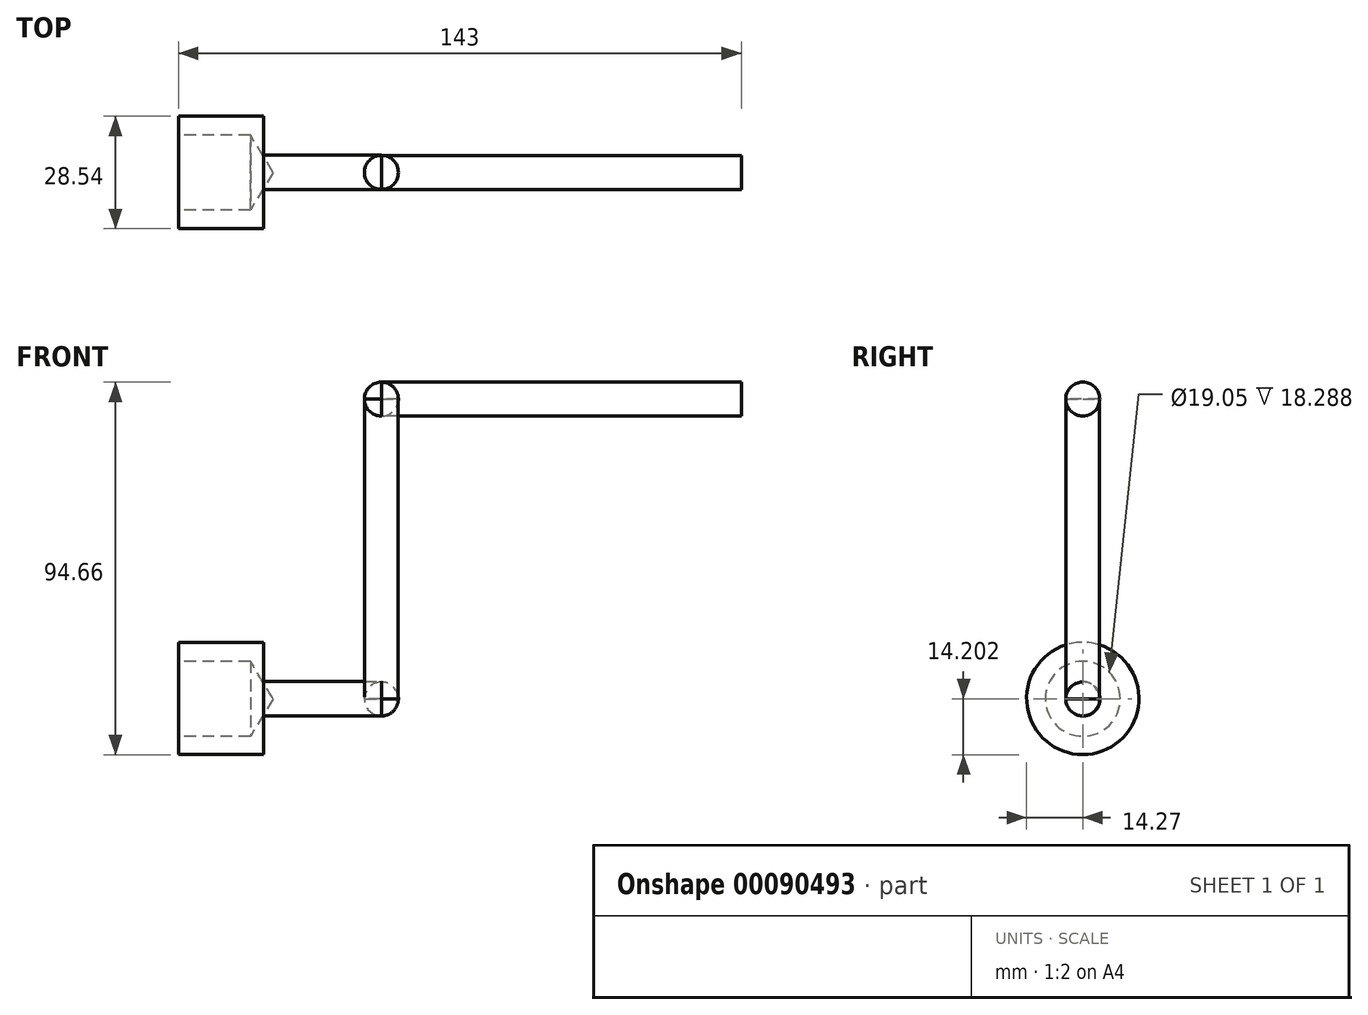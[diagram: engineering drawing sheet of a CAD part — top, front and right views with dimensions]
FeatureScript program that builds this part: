
annotation { "Feature Type Name" : "Feature", "Feature Type Description" : "" }
export const myFeature = defineFeature(function(context is Context, id is Id, definition is map)
    precondition{}
    {
        {
            var Q0;
            Q0=qCreatedBy(makeId("Right.planeOp"),FACE);
            var sketch = newSketch(context, id + "F0", { "sketchPlane" : qUnion([Q0])});
            skCircle(sketch, "E0", {"center": v(0, 45.27) * mm, "radius": 4.32 * mm});
            skLineSegment(sketch, "E1", {"start": v(0, 40.95) * mm, "end": v(0, 49.59) * mm});
            skSolve(sketch);
        }
        {
            var Q0;
            Q0=qCreatedBy(makeId("Right.planeOp"),FACE);
            cPlane(context, id + "F1", {"entities" : qUnion([Q0]), "cplaneType" : CPlaneType.OFFSET, "offset" : 91.44 * mm, "width" : 152.4 * mm, "height" : 152.4 * mm});
        }
        {
            var Q0;
            Q0=qCreatedBy(id+"F1.planeOp",FACE);
            var sketch = newSketch(context, id + "F2", { "sketchPlane" : qUnion([Q0])});
            skCircle(sketch, "E2", {"center": v(0.04, 45.27) * mm, "radius": 3.16 * mm});
            skPoint(sketch, "E2.first.point", {"position": v(0, 48.43) * mm});
            skPoint(sketch, "E2.second.point", {"position": v(0, 42.11) * mm});
            skPoint(sketch, "E2.third.point", {"position": v(3.16, 45.8) * mm});
            skSolve(sketch);
        }
        {
            var Q0;
            {var subQ0=sQuery(id+"F0.wireOp",EDGE,"E1");Q0=makeQuery(id+"F0.imprint","IMPRINT",FACE,{"disambiguationData":[TD([[makeQuery(id+"F0.imprint","IMPRINT",EDGE,{"derivedFrom":subQ0}),-1.0]])]});}
            var Q1;
            {var subQ0=sQuery(id+"F0.wireOp",EDGE,"E1");Q1=makeQuery(id+"F0.imprint","IMPRINT",FACE,{"disambiguationData":[TD([[makeQuery(id+"F0.imprint","IMPRINT",EDGE,{"derivedFrom":subQ0}),1.0]])]});}
            var Q2;
            Q2=sQuery(id+"F0.wireOp",EDGE,"E0");
            extrude(context, id + "F3", {"entities" : qUnion([Q0, Q1]), "surfaceEntities" : qUnion([Q2]), "depth" : 91.44 * mm});
        }
        {
            var Q0;
            {var subQ0=sQuery(id+"F0.wireOp",EDGE,"E1");Q0=makeQuery(id+"F0.imprint","IMPRINT",FACE,{"disambiguationData":[TD([[makeQuery(id+"F0.imprint","IMPRINT",EDGE,{"derivedFrom":subQ0}),1.0]])]});}
            var Q1;
            Q1=sQuery(id+"F0.wireOp",EDGE,"E1");
            revolve(context, id + "F4", {"entities" : qUnion([Q0]), "axis" : qUnion([Q1]), "revolveType" : RevolveType.FULL});
        }
        {
            var Q0;
            Q0=qCreatedBy(makeId("Top.planeOp"),FACE);
            cPlane(context, id + "F5", {"entities" : qUnion([Q0]), "cplaneType" : CPlaneType.OFFSET, "offset" : 45.27 * mm, "width" : 152.4 * mm, "height" : 152.4 * mm});
        }
        {
            var Q0;
            Q0=qCreatedBy(id+"F5.planeOp",FACE);
            var sketch = newSketch(context, id + "F6", { "sketchPlane" : qUnion([Q0])});
            skCircle(sketch, "E3", {"center": v(0, 0) * mm, "radius": 4.29 * mm});
            skSolve(sketch);
        }
        {
            var Q0;
            Q0 = qSketchRegion(id + "F6", true);
            extrude(context, id + "F7", {"entities" : qUnion([Q0]), "oppositeDirection" : true, "depth" : 76.2 * mm});
        }
        {
            var Q0;
            Q0=makeQuery(id+"F4.opRevolve","SWEPT_BODY",BODY,{"disambiguationData":[OSD([sQuery(id+"F0.wireOp",EDGE,"E0"),sQuery(id+"F0.wireOp",EDGE,"E1")])]});
            transform(context, id + "F8", {"entities" : qUnion([Q0]), "transformType" : TransformType.TRANSLATION_3D, "dx" : 0 * mm, "dy" : 0 * mm, "dz" : -76.2 * mm, "makeCopy" : true});
        }
        {
            var Q0;
            Q0=qCreatedBy(makeId("Right.planeOp"),FACE);
            var sketch = newSketch(context, id + "F9", { "sketchPlane" : qUnion([Q0])});
            skCircle(sketch, "E4", {"center": v(0, -30.9) * mm, "radius": 4.37 * mm});
            skPoint(sketch, "E4.first.point", {"position": v(0, -35.26) * mm});
            skPoint(sketch, "E4.second.point", {"position": v(-3.92, -32.8) * mm});
            skPoint(sketch, "E4.third.point", {"position": v(3.7, -33.22) * mm});
            skSolve(sketch);
        }
        {
            var Q0;
            Q0=qCreatedBy(makeId("Right.planeOp"),FACE);
            cPlane(context, id + "F10", {"entities" : qUnion([Q0]), "cplaneType" : CPlaneType.OFFSET, "offset" : 51.56 * mm, "oppositeDirection" : true, "width" : 152.4 * mm, "height" : 152.4 * mm});
        }
        {
            var Q0;
            Q0=qCreatedBy(id+"F10.planeOp",FACE);
            var sketch = newSketch(context, id + "F11", { "sketchPlane" : qUnion([Q0])});
            skCircle(sketch, "E5", {"center": v(0, -30.87) * mm, "radius": 14.27 * mm});
            skSolve(sketch);
        }
        {
            var Q0;
            Q0=qCreatedBy(id+"F10.planeOp",FACE);
            cPlane(context, id + "F12", {"entities" : qUnion([Q0]), "cplaneType" : CPlaneType.OFFSET, "offset" : 21.59 * mm, "width" : 152.4 * mm, "height" : 152.4 * mm});
        }
        {
            var Q0;
            Q0=qCreatedBy(id+"F12.planeOp",FACE);
            var sketch = newSketch(context, id + "F13", { "sketchPlane" : qUnion([Q0])});
            skCircle(sketch, "E6", {"center": v(0, -30.8) * mm, "radius": 14.27 * mm});
            skSolve(sketch);
        }
        {
            var Q0;
            Q0 = qSketchRegion(id + "F9", true);
            var Q1;
            Q1=sQuery(id+"F9.wireOp",EDGE,"E4");
            extrude(context, id + "F14", {"entities" : qUnion([Q0]), "surfaceEntities" : qUnion([Q1]), "oppositeDirection" : true, "depth" : 29.97 * mm});
        }
        {
            var Q0;
            Q0=makeQuery(id+"F13.imprint","IMPRINT",FACE,{"disambiguationData":[TD([[makeQuery(id+"F13.imprint","IMPRINT",EDGE,{"derivedFrom":sQuery(id+"F13.wireOp",EDGE,"E6")}),1.0]])]});
            extrude(context, id + "F15", {"entities" : qUnion([Q0]), "operationType" : NewBodyOperationType.ADD, "oppositeDirection" : true, "depth" : 21.59 * mm});
        }
        {
            var Q0;
            Q0=sQuery(id+"F11.wireOp",VERTEX,"E5.center");
            var Q1;
            Q1=makeQuery(id+"F14.opExtrude","SWEPT_BODY",BODY,{"disambiguationData":[OSD([sQuery(id+"F9.wireOp",EDGE,"E4")])]});
            hole(context, id + "F16", {"style" : HoleStyle.SIMPLE, "endStyle" : HoleEndStyle.BLIND, "oppositeDirection" : true, "holeDiameter" : 19.05 * mm, "holeDepth" : 18.29 * mm, "startFromSketch" : true, "locations" : qUnion([Q0]), "scope" : qUnion([Q1])});
        }
    });
